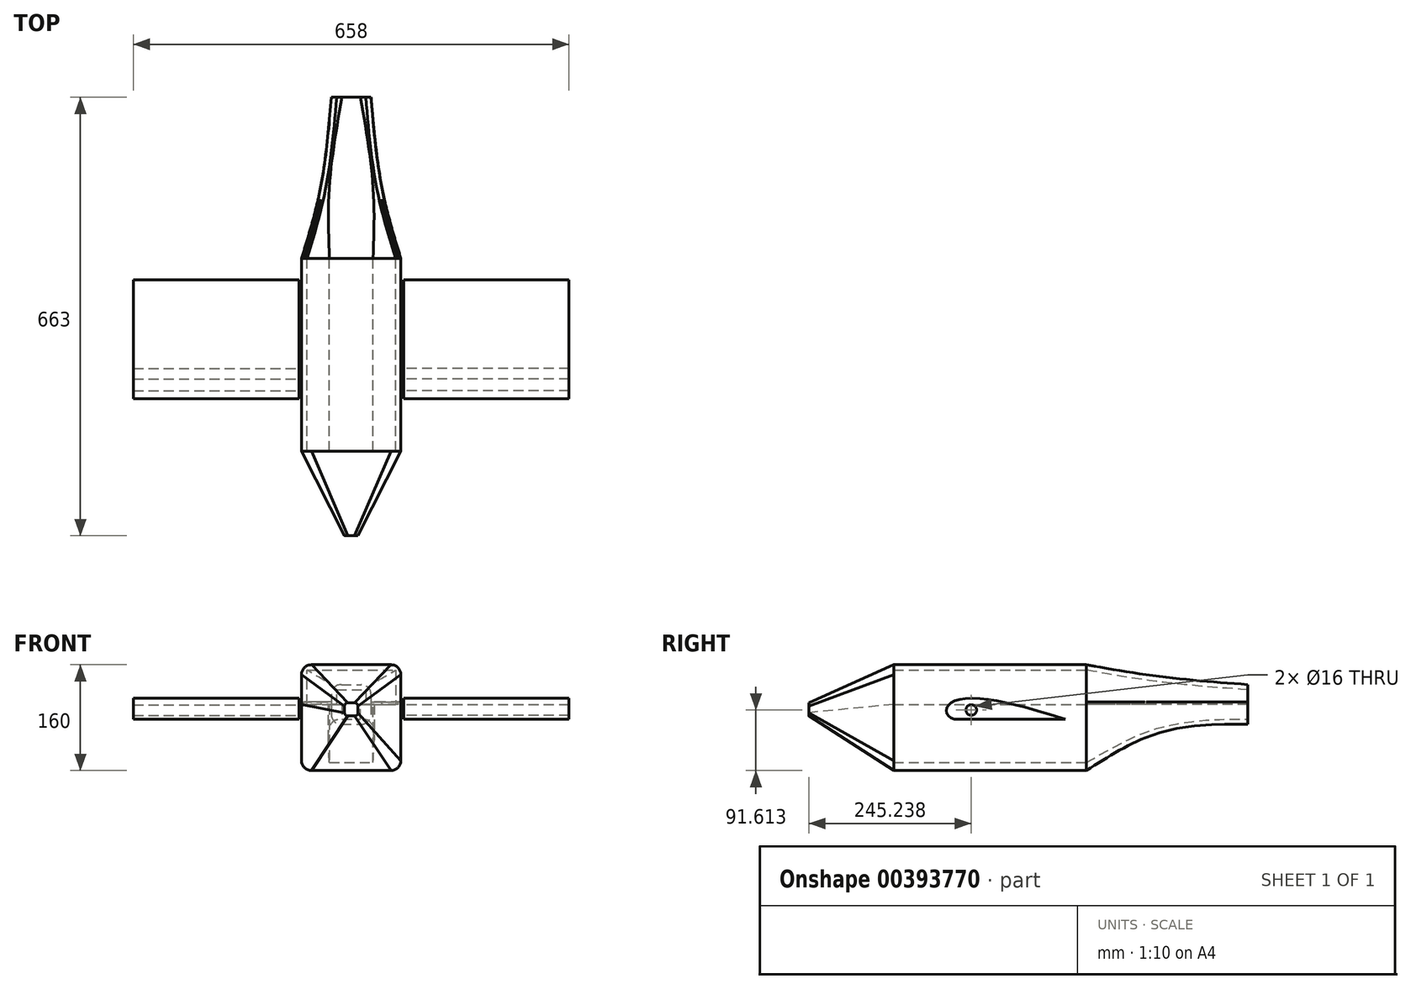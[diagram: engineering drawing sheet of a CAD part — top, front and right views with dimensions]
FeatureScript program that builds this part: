
annotation { "Feature Type Name" : "Feature", "Feature Type Description" : "" }
export const myFeature = defineFeature(function(context is Context, id is Id, definition is map)
    precondition{}
    {
        {
            var Q0;
            Q0=qCreatedBy(makeId("Front.planeOp"),FACE);
            cPlane(context, id + "F0", {"entities" : qUnion([Q0]), "cplaneType" : CPlaneType.OFFSET, "offset" : 154 * mm, "oppositeDirection" : true, "width" : 150 * mm, "height" : 150 * mm});
        }
        {
            var Q0;
            Q0=qCreatedBy(id+"F0.planeOp",FACE);
            var sketch = newSketch(context, id + "F1", { "sketchPlane" : qUnion([Q0])});
            skLineSegment(sketch, "E0.bottom", {"start": v(-15, 37.5) * mm, "end": v(15, 37.5) * mm});
            skLineSegment(sketch, "E0.top", {"start": v(-26, 7.5) * mm, "end": v(-14, 7.5) * mm});
            skLineSegment(sketch, "E0.left", {"start": v(-30, 22.5) * mm, "end": v(-30, 7.5) * mm});
            skLineSegment(sketch, "E0.right", {"start": v(30, 22.5) * mm, "end": v(30, 7.5) * mm});
            skLineSegment(sketch, "E1", {"start": v(0, 97.44) * mm, "end": v(0, -97.44) * mm, "construction": true});
            skLineSegment(sketch, "E2", {"start": v(-121.5, 0) * mm, "end": v(121.5, 0) * mm, "construction": true});
            skPoint(sketch, "E3", {"position": v(0, 0) * mm});
            skPoint(sketch, "E4", {"position": v(0, 37.5) * mm});
            skPoint(sketch, "E5.visualSharp", {"position": v(-30, 37.5) * mm});
            skArc(sketch, "E5.filletArc", {"start": v(-15, 37.5) * mm, "mid": v(-25.6, 33.1) * mm, "end": v(-30, 22.5) * mm});
            skPoint(sketch, "E6.visualSharp", {"position": v(30, 37.5) * mm});
            skArc(sketch, "E6.filletArc", {"start": v(30, 22.5) * mm, "mid": v(25.6, 33.1) * mm, "end": v(15, 37.5) * mm});
            skLineSegment(sketch, "E7", {"start": v(-22, 7.5) * mm, "end": v(-22, 29.5) * mm});
            skLineSegment(sketch, "E8", {"start": v(-22, 29.5) * mm, "end": v(22, 29.5) * mm});
            skLineSegment(sketch, "E9", {"start": v(22, 29.5) * mm, "end": v(22, 7.5) * mm});
            skPoint(sketch, "E10", {"position": v(0, 29.5) * mm});
            skLineSegment(sketch, "E11", {"start": v(-26, 7.5) * mm, "end": v(-26, 11.5) * mm});
            skLineSegment(sketch, "E12", {"start": v(-26, 11.5) * mm, "end": v(-30, 11.5) * mm});
            skLineSegment(sketch, "E13", {"start": v(26, 7.5) * mm, "end": v(26, 11.5) * mm});
            skLineSegment(sketch, "E14", {"start": v(26, 11.5) * mm, "end": v(30, 11.5) * mm});
            skLineSegment(sketch, "E15.top", {"start": v(-15, -22.5) * mm, "end": v(15, -22.5) * mm});
            skLineSegment(sketch, "E15.left", {"start": v(-30, 7.5) * mm, "end": v(-30, -7.5) * mm});
            skLineSegment(sketch, "E15.right", {"start": v(30, 7.5) * mm, "end": v(30, -7.5) * mm});
            skLineSegment(sketch, "E16", {"start": v(-14, 7.5) * mm, "end": v(-14, -14.5) * mm});
            skLineSegment(sketch, "E17", {"start": v(-14, -14.5) * mm, "end": v(14, -14.5) * mm});
            skLineSegment(sketch, "E18", {"start": v(14, -14.5) * mm, "end": v(14, 7.5) * mm});
            skPoint(sketch, "E19", {"position": v(0, -14.5) * mm});
            skPoint(sketch, "E20", {"position": v(0, -22.5) * mm});
            skPoint(sketch, "E21.visualSharp", {"position": v(-30, -22.5) * mm});
            skArc(sketch, "E21.filletArc", {"start": v(-30, -7.5) * mm, "mid": v(-25.6, -18.11) * mm, "end": v(-15, -22.5) * mm});
            skPoint(sketch, "E22.visualSharp", {"position": v(30, -22.5) * mm});
            skArc(sketch, "E22.filletArc", {"start": v(15, -22.5) * mm, "mid": v(25.6, -18.11) * mm, "end": v(30, -7.5) * mm});
            skLineSegment(sketch, "E23.trimOffspring", {"start": v(14, 7.5) * mm, "end": v(26, 7.5) * mm});
            skSolve(sketch);
        }
        {
            var Q0;
            Q0=qCreatedBy(makeId("Front.planeOp"),FACE);
            cPlane(context, id + "F2", {"entities" : qUnion([Q0]), "cplaneType" : CPlaneType.OFFSET, "offset" : 90 * mm, "width" : 150 * mm, "height" : 150 * mm});
        }
        {
            var Q0;
            Q0=qCreatedBy(id+"F2.planeOp",FACE);
            cPlane(context, id + "F3", {"entities" : qUnion([Q0]), "cplaneType" : CPlaneType.OFFSET, "offset" : 111 * mm, "width" : 150 * mm, "height" : 150 * mm});
        }
        {
            var Q0;
            Q0=qCreatedBy(id+"F3.planeOp",FACE);
            cPlane(context, id + "F4", {"entities" : qUnion([Q0]), "cplaneType" : CPlaneType.OFFSET, "offset" : 180 * mm, "width" : 150 * mm, "height" : 150 * mm});
        }
        {
            var Q0;
            Q0=qCreatedBy(makeId("Front.planeOp"),FACE);
            var sketch = newSketch(context, id + "F5", { "sketchPlane" : qUnion([Q0])});
            skLineSegment(sketch, "E24.bottom", {"start": v(-35, 52.5) * mm, "end": v(35, 52.5) * mm});
            skLineSegment(sketch, "E24.top", {"start": v(-46, 7.5) * mm, "end": v(-34, 7.5) * mm});
            skLineSegment(sketch, "E24.left", {"start": v(-50, 37.5) * mm, "end": v(-50, 7.5) * mm});
            skLineSegment(sketch, "E24.right", {"start": v(50, 37.5) * mm, "end": v(50, 7.5) * mm});
            skLineSegment(sketch, "E25", {"start": v(0, 97.44) * mm, "end": v(0, -97.44) * mm, "construction": true});
            skLineSegment(sketch, "E26", {"start": v(-121.5, 0) * mm, "end": v(121.5, 0) * mm, "construction": true});
            skPoint(sketch, "E27", {"position": v(0, 0) * mm});
            skPoint(sketch, "E28", {"position": v(0, 52.5) * mm});
            skPoint(sketch, "E29.visualSharp", {"position": v(-50, 52.5) * mm});
            skArc(sketch, "E29.filletArc", {"start": v(-35, 52.5) * mm, "mid": v(-45.6, 48.1) * mm, "end": v(-50, 37.5) * mm});
            skPoint(sketch, "E30.visualSharp", {"position": v(50, 52.5) * mm});
            skArc(sketch, "E30.filletArc", {"start": v(50, 37.5) * mm, "mid": v(45.6, 48.1) * mm, "end": v(35, 52.5) * mm});
            skLineSegment(sketch, "E31", {"start": v(-42, 7.5) * mm, "end": v(-42, 44.5) * mm});
            skLineSegment(sketch, "E32", {"start": v(-42, 44.5) * mm, "end": v(42, 44.5) * mm});
            skLineSegment(sketch, "E33", {"start": v(42, 44.5) * mm, "end": v(42, 7.5) * mm});
            skPoint(sketch, "E34", {"position": v(0, 44.5) * mm});
            skLineSegment(sketch, "E35", {"start": v(-46, 7.5) * mm, "end": v(-46, 11.5) * mm});
            skLineSegment(sketch, "E36", {"start": v(-46, 11.5) * mm, "end": v(-50, 11.5) * mm});
            skLineSegment(sketch, "E37", {"start": v(46, 7.5) * mm, "end": v(46, 11.5) * mm});
            skLineSegment(sketch, "E38", {"start": v(46, 11.5) * mm, "end": v(50, 11.5) * mm});
            skLineSegment(sketch, "E39.top", {"start": v(-35, -42.5) * mm, "end": v(35, -42.5) * mm});
            skLineSegment(sketch, "E39.left", {"start": v(-50, 7.5) * mm, "end": v(-50, -27.5) * mm});
            skLineSegment(sketch, "E39.right", {"start": v(50, 7.5) * mm, "end": v(50, -27.5) * mm});
            skLineSegment(sketch, "E40", {"start": v(-34, 7.5) * mm, "end": v(-34, -34.5) * mm});
            skLineSegment(sketch, "E41", {"start": v(-34, -34.5) * mm, "end": v(34, -34.5) * mm});
            skLineSegment(sketch, "E42", {"start": v(34, -34.5) * mm, "end": v(34, 7.5) * mm});
            skPoint(sketch, "E43", {"position": v(0, -34.5) * mm});
            skPoint(sketch, "E44", {"position": v(0, -42.5) * mm});
            skPoint(sketch, "E45.visualSharp", {"position": v(-50, -42.5) * mm});
            skArc(sketch, "E45.filletArc", {"start": v(-50, -27.5) * mm, "mid": v(-45.6, -38.11) * mm, "end": v(-35, -42.5) * mm});
            skPoint(sketch, "E46.visualSharp", {"position": v(50, -42.5) * mm});
            skArc(sketch, "E46.filletArc", {"start": v(35, -42.5) * mm, "mid": v(45.6, -38.11) * mm, "end": v(50, -27.5) * mm});
            skLineSegment(sketch, "E47.trimOffspring", {"start": v(34, 7.5) * mm, "end": v(46, 7.5) * mm});
            skSolve(sketch);
        }
        {
            var Q0;
            Q0=qCreatedBy(id+"F2.planeOp",FACE);
            var sketch = newSketch(context, id + "F6", { "sketchPlane" : qUnion([Q0])});
            skLineSegment(sketch, "E48.bottom", {"start": v(-60, 67.5) * mm, "end": v(60, 67.5) * mm});
            skLineSegment(sketch, "E48.top", {"start": v(-71, 7.5) * mm, "end": v(-33, 7.5) * mm});
            skLineSegment(sketch, "E48.left", {"start": v(-75, 52.5) * mm, "end": v(-75, 7.5) * mm});
            skLineSegment(sketch, "E48.right", {"start": v(75, 52.5) * mm, "end": v(75, 7.5) * mm});
            skLineSegment(sketch, "E49", {"start": v(0, 97.44) * mm, "end": v(0, -97.44) * mm, "construction": true});
            skLineSegment(sketch, "E50", {"start": v(-121.5, 0) * mm, "end": v(121.5, 0) * mm, "construction": true});
            skPoint(sketch, "E51", {"position": v(0, 0) * mm});
            skPoint(sketch, "E52", {"position": v(0, 67.5) * mm});
            skPoint(sketch, "E53.visualSharp", {"position": v(-75, 67.5) * mm});
            skArc(sketch, "E53.filletArc", {"start": v(-60, 67.5) * mm, "mid": v(-70.6, 63.1) * mm, "end": v(-75, 52.5) * mm});
            skPoint(sketch, "E54.visualSharp", {"position": v(75, 67.5) * mm});
            skArc(sketch, "E54.filletArc", {"start": v(75, 52.5) * mm, "mid": v(70.6, 63.1) * mm, "end": v(60, 67.5) * mm});
            skLineSegment(sketch, "E55", {"start": v(-67, 7.5) * mm, "end": v(-67, 59.5) * mm});
            skLineSegment(sketch, "E56", {"start": v(-67, 59.5) * mm, "end": v(67, 59.5) * mm});
            skLineSegment(sketch, "E57", {"start": v(67, 59.5) * mm, "end": v(67, 7.5) * mm});
            skPoint(sketch, "E58", {"position": v(0, 59.5) * mm});
            skLineSegment(sketch, "E59", {"start": v(-71, 7.5) * mm, "end": v(-71, 11.5) * mm});
            skLineSegment(sketch, "E60", {"start": v(-71, 11.5) * mm, "end": v(-75, 11.5) * mm});
            skLineSegment(sketch, "E61", {"start": v(71, 7.5) * mm, "end": v(71, 11.5) * mm});
            skLineSegment(sketch, "E62", {"start": v(71, 11.5) * mm, "end": v(75, 11.5) * mm});
            skLineSegment(sketch, "E63.top", {"start": v(-60, -92.5) * mm, "end": v(60, -92.5) * mm});
            skLineSegment(sketch, "E63.left", {"start": v(-75, 7.5) * mm, "end": v(-75, -77.5) * mm});
            skLineSegment(sketch, "E63.right", {"start": v(75, 7.5) * mm, "end": v(75, -77.5) * mm});
            skLineSegment(sketch, "E64", {"start": v(-33, 7.5) * mm, "end": v(-33, -80.5) * mm});
            skLineSegment(sketch, "E65", {"start": v(-33, -80.5) * mm, "end": v(33, -80.5) * mm});
            skLineSegment(sketch, "E66", {"start": v(33, -80.5) * mm, "end": v(33, 7.5) * mm});
            skPoint(sketch, "E67", {"position": v(0, -80.5) * mm});
            skPoint(sketch, "E68", {"position": v(0, -92.5) * mm});
            skPoint(sketch, "E69.visualSharp", {"position": v(-75, -92.5) * mm});
            skArc(sketch, "E69.filletArc", {"start": v(-75, -77.5) * mm, "mid": v(-70.6, -88.11) * mm, "end": v(-60, -92.5) * mm});
            skPoint(sketch, "E70.visualSharp", {"position": v(75, -92.5) * mm});
            skArc(sketch, "E70.filletArc", {"start": v(60, -92.5) * mm, "mid": v(70.6, -88.11) * mm, "end": v(75, -77.5) * mm});
            skLineSegment(sketch, "E71.trimOffspring", {"start": v(33, 7.5) * mm, "end": v(71, 7.5) * mm});
            skSolve(sketch);
        }
        {
            var Q0;
            Q0=qCreatedBy(id+"F3.planeOp",FACE);
            var sketch = newSketch(context, id + "F7", { "sketchPlane" : qUnion([Q0])});
            skLineSegment(sketch, "E72.bottom", {"start": v(-60, 67.5) * mm, "end": v(60, 67.5) * mm});
            skLineSegment(sketch, "E72.top", {"start": v(-71, 7.5) * mm, "end": v(-33, 7.5) * mm});
            skLineSegment(sketch, "E72.left", {"start": v(-75, 52.5) * mm, "end": v(-75, 7.5) * mm});
            skLineSegment(sketch, "E72.right", {"start": v(75, 52.5) * mm, "end": v(75, 7.5) * mm});
            skLineSegment(sketch, "E73", {"start": v(0, 97.44) * mm, "end": v(0, -97.44) * mm, "construction": true});
            skLineSegment(sketch, "E74", {"start": v(-121.5, 0) * mm, "end": v(121.5, 0) * mm, "construction": true});
            skPoint(sketch, "E75", {"position": v(0, 0) * mm});
            skPoint(sketch, "E76", {"position": v(0, 67.5) * mm});
            skPoint(sketch, "E77.visualSharp", {"position": v(-75, 67.5) * mm});
            skArc(sketch, "E77.filletArc", {"start": v(-60, 67.5) * mm, "mid": v(-70.6, 63.1) * mm, "end": v(-75, 52.5) * mm});
            skPoint(sketch, "E78.visualSharp", {"position": v(75, 67.5) * mm});
            skArc(sketch, "E78.filletArc", {"start": v(75, 52.5) * mm, "mid": v(70.6, 63.1) * mm, "end": v(60, 67.5) * mm});
            skLineSegment(sketch, "E79", {"start": v(-67, 7.5) * mm, "end": v(-67, 59.5) * mm});
            skLineSegment(sketch, "E80", {"start": v(-67, 59.5) * mm, "end": v(67, 59.5) * mm});
            skLineSegment(sketch, "E81", {"start": v(67, 59.5) * mm, "end": v(67, 7.5) * mm});
            skPoint(sketch, "E82", {"position": v(0, 59.5) * mm});
            skLineSegment(sketch, "E83", {"start": v(-71, 7.5) * mm, "end": v(-71, 11.5) * mm});
            skLineSegment(sketch, "E84", {"start": v(-71, 11.5) * mm, "end": v(-75, 11.5) * mm});
            skLineSegment(sketch, "E85", {"start": v(71, 7.5) * mm, "end": v(71, 11.5) * mm});
            skLineSegment(sketch, "E86", {"start": v(71, 11.5) * mm, "end": v(75, 11.5) * mm});
            skLineSegment(sketch, "E87.top", {"start": v(-60, -92.5) * mm, "end": v(60, -92.5) * mm});
            skLineSegment(sketch, "E87.left", {"start": v(-75, 7.5) * mm, "end": v(-75, -77.5) * mm});
            skLineSegment(sketch, "E87.right", {"start": v(75, 7.5) * mm, "end": v(75, -77.5) * mm});
            skLineSegment(sketch, "E88", {"start": v(-33, 7.5) * mm, "end": v(-33, -80.5) * mm});
            skLineSegment(sketch, "E89", {"start": v(-33, -80.5) * mm, "end": v(33, -80.5) * mm});
            skLineSegment(sketch, "E90", {"start": v(33, -80.5) * mm, "end": v(33, 7.5) * mm});
            skPoint(sketch, "E91", {"position": v(0, -80.5) * mm});
            skPoint(sketch, "E92", {"position": v(0, -92.5) * mm});
            skPoint(sketch, "E93.visualSharp", {"position": v(-75, -92.5) * mm});
            skArc(sketch, "E93.filletArc", {"start": v(-75, -77.5) * mm, "mid": v(-70.6, -88.11) * mm, "end": v(-60, -92.5) * mm});
            skPoint(sketch, "E94.visualSharp", {"position": v(75, -92.5) * mm});
            skArc(sketch, "E94.filletArc", {"start": v(60, -92.5) * mm, "mid": v(70.6, -88.11) * mm, "end": v(75, -77.5) * mm});
            skLineSegment(sketch, "E95.trimOffspring", {"start": v(33, 7.5) * mm, "end": v(71, 7.5) * mm});
            skSolve(sketch);
        }
        {
            var Q0;
            Q0=qCreatedBy(id+"F4.planeOp",FACE);
            var sketch = newSketch(context, id + "F8", { "sketchPlane" : qUnion([Q0])});
            skLineSegment(sketch, "E96.bottom", {"start": v(-60, 67.5) * mm, "end": v(60, 67.5) * mm});
            skLineSegment(sketch, "E96.top", {"start": v(-71, 7.5) * mm, "end": v(-33, 7.5) * mm});
            skLineSegment(sketch, "E96.left", {"start": v(-75, 52.5) * mm, "end": v(-75, 7.5) * mm});
            skLineSegment(sketch, "E96.right", {"start": v(75, 52.5) * mm, "end": v(75, 7.5) * mm});
            skLineSegment(sketch, "E97", {"start": v(0, 97.44) * mm, "end": v(0, -97.44) * mm, "construction": true});
            skLineSegment(sketch, "E98", {"start": v(-121.5, 0) * mm, "end": v(121.5, 0) * mm, "construction": true});
            skPoint(sketch, "E99", {"position": v(0, 0) * mm});
            skPoint(sketch, "E100", {"position": v(0, 67.5) * mm});
            skPoint(sketch, "E101.visualSharp", {"position": v(-75, 67.5) * mm});
            skArc(sketch, "E101.filletArc", {"start": v(-60, 67.5) * mm, "mid": v(-70.6, 63.1) * mm, "end": v(-75, 52.5) * mm});
            skPoint(sketch, "E102.visualSharp", {"position": v(75, 67.5) * mm});
            skArc(sketch, "E102.filletArc", {"start": v(75, 52.5) * mm, "mid": v(70.6, 63.1) * mm, "end": v(60, 67.5) * mm});
            skLineSegment(sketch, "E103", {"start": v(-67, 7.5) * mm, "end": v(-67, 59.5) * mm});
            skLineSegment(sketch, "E104", {"start": v(-67, 59.5) * mm, "end": v(67, 59.5) * mm});
            skLineSegment(sketch, "E105", {"start": v(67, 59.5) * mm, "end": v(67, 7.5) * mm});
            skPoint(sketch, "E106", {"position": v(0, 59.5) * mm});
            skLineSegment(sketch, "E107", {"start": v(-71, 7.5) * mm, "end": v(-71, 11.5) * mm});
            skLineSegment(sketch, "E108", {"start": v(-71, 11.5) * mm, "end": v(-75, 11.5) * mm});
            skLineSegment(sketch, "E109", {"start": v(71, 7.5) * mm, "end": v(71, 11.5) * mm});
            skLineSegment(sketch, "E110", {"start": v(71, 11.5) * mm, "end": v(75, 11.5) * mm});
            skLineSegment(sketch, "E111.top", {"start": v(-60, -92.5) * mm, "end": v(60, -92.5) * mm});
            skLineSegment(sketch, "E111.left", {"start": v(-75, 7.5) * mm, "end": v(-75, -77.5) * mm});
            skLineSegment(sketch, "E111.right", {"start": v(75, 7.5) * mm, "end": v(75, -77.5) * mm});
            skLineSegment(sketch, "E112", {"start": v(-33, 7.5) * mm, "end": v(-33, -80.5) * mm});
            skLineSegment(sketch, "E113", {"start": v(-33, -80.5) * mm, "end": v(33, -80.5) * mm});
            skLineSegment(sketch, "E114", {"start": v(33, -80.5) * mm, "end": v(33, 7.5) * mm});
            skPoint(sketch, "E115", {"position": v(0, -80.5) * mm});
            skPoint(sketch, "E116", {"position": v(0, -92.5) * mm});
            skPoint(sketch, "E117.visualSharp", {"position": v(-75, -92.5) * mm});
            skArc(sketch, "E117.filletArc", {"start": v(-75, -77.5) * mm, "mid": v(-70.6, -88.11) * mm, "end": v(-60, -92.5) * mm});
            skPoint(sketch, "E118.visualSharp", {"position": v(75, -92.5) * mm});
            skArc(sketch, "E118.filletArc", {"start": v(60, -92.5) * mm, "mid": v(70.6, -88.11) * mm, "end": v(75, -77.5) * mm});
            skLineSegment(sketch, "E119.trimOffspring", {"start": v(33, 7.5) * mm, "end": v(71, 7.5) * mm});
            skSolve(sketch);
        }
        {
            var Q0;
            Q0=makeQuery(id+"F1.imprint","IMPRINT",FACE,{"disambiguationData":[TD([[makeQuery(id+"F1.imprint","IMPRINT",EDGE,{"derivedFrom":sQuery(id+"F1.wireOp",EDGE,"E0.bottom")}),-1.0]])]});
            var Q1;
            Q1=makeQuery(id+"F5.imprint","IMPRINT",FACE,{"disambiguationData":[TD([[makeQuery(id+"F5.imprint","IMPRINT",EDGE,{"derivedFrom":sQuery(id+"F5.wireOp",EDGE,"E24.bottom")}),-1.0]])]});
            var Q2;
            Q2=makeQuery(id+"F6.imprint","IMPRINT",FACE,{"disambiguationData":[TD([[makeQuery(id+"F6.imprint","IMPRINT",EDGE,{"derivedFrom":sQuery(id+"F6.wireOp",EDGE,"E48.bottom")}),-1.0]])]});
            loft(context, id + "F9", {"sheetProfilesArray" : [{ "sheetProfileEntities" : qUnion([Q0]) }, { "sheetProfileEntities" : qUnion([Q1]) }, { "sheetProfileEntities" : qUnion([Q2]) }]});
        }
        {
            var Q0;
            Q0=makeQuery(id+"F8.imprint","IMPRINT",FACE,{"disambiguationData":[TD([[makeQuery(id+"F8.imprint","IMPRINT",EDGE,{"derivedFrom":sQuery(id+"F8.wireOp",EDGE,"E96.bottom")}),-1.0]])]});
            var Q1;
            Q1=makeQuery(id+"F7.imprint","IMPRINT",FACE,{"disambiguationData":[TD([[makeQuery(id+"F7.imprint","IMPRINT",EDGE,{"derivedFrom":sQuery(id+"F7.wireOp",EDGE,"E72.bottom")}),-1.0]])]});
            var Q2;
            Q2=makeQuery(id+"F6.imprint","IMPRINT",FACE,{"disambiguationData":[TD([[makeQuery(id+"F6.imprint","IMPRINT",EDGE,{"derivedFrom":sQuery(id+"F6.wireOp",EDGE,"E48.bottom")}),-1.0]])]});
            loft(context, id + "F10", {"sheetProfilesArray" : [{ "sheetProfileEntities" : qUnion([Q0]) }, { "sheetProfileEntities" : qUnion([Q1]) }, { "sheetProfileEntities" : qUnion([Q2]) }]});
        }
        {
            var Q1;
            {var subQ3=sQuery(id+"F8.wireOp",EDGE,"E107");Q1=makeQuery(id+"F8.imprint","IMPRINT",FACE,{"disambiguationData":[TD([[makeQuery(id+"F8.imprint","IMPRINT",EDGE,{"derivedFrom":subQ3}),1.0]])]});}
            var Q2;
            {var subQ3=sQuery(id+"F7.wireOp",EDGE,"E83");Q2=makeQuery(id+"F7.imprint","IMPRINT",FACE,{"disambiguationData":[TD([[makeQuery(id+"F7.imprint","IMPRINT",EDGE,{"derivedFrom":subQ3}),1.0]])]});}
            var Q3;
            {var subQ3=sQuery(id+"F6.wireOp",EDGE,"E59");Q3=makeQuery(id+"F6.imprint","IMPRINT",FACE,{"disambiguationData":[TD([[makeQuery(id+"F6.imprint","IMPRINT",EDGE,{"derivedFrom":subQ3}),1.0]])]});}
            loft(context, id + "F11", {"sheetProfilesArray" : [{ "sheetProfileEntities" : qUnion([Q1]) }, { "sheetProfileEntities" : qUnion([Q2]) }, { "sheetProfileEntities" : qUnion([Q3]) }]});
        }
        {
            var Q1;
            {var subQ3=sQuery(id+"F6.wireOp",EDGE,"E59");Q1=makeQuery(id+"F6.imprint","IMPRINT",FACE,{"disambiguationData":[TD([[makeQuery(id+"F6.imprint","IMPRINT",EDGE,{"derivedFrom":subQ3}),1.0]])]});}
            var Q2;
            {var subQ3=sQuery(id+"F5.wireOp",EDGE,"E35");Q2=makeQuery(id+"F5.imprint","IMPRINT",FACE,{"disambiguationData":[TD([[makeQuery(id+"F5.imprint","IMPRINT",EDGE,{"derivedFrom":subQ3}),1.0]])]});}
            var Q3;
            {var subQ3=sQuery(id+"F1.wireOp",EDGE,"E11");Q3=makeQuery(id+"F1.imprint","IMPRINT",FACE,{"disambiguationData":[TD([[makeQuery(id+"F1.imprint","IMPRINT",EDGE,{"derivedFrom":subQ3}),1.0]])]});}
            loft(context, id + "F12", {"operationType" : NewBodyOperationType.ADD, "sheetProfilesArray" : [{ "sheetProfileEntities" : qUnion([Q1]) }, { "sheetProfileEntities" : qUnion([Q2]) }, { "sheetProfileEntities" : qUnion([Q3]) }]});
        }
        {
            var Q0;
            Q0=qCreatedBy(id+"F4.planeOp",FACE);
            cPlane(context, id + "F13", {"entities" : qUnion([Q0]), "cplaneType" : CPlaneType.OFFSET, "offset" : 0 * mm, "width" : 150 * mm, "height" : 150 * mm});
        }
        {
            var Q0;
            Q0=qCreatedBy(id+"F13.planeOp",FACE);
            cPlane(context, id + "F14", {"entities" : qUnion([Q0]), "cplaneType" : CPlaneType.OFFSET, "offset" : 128 * mm, "width" : 150 * mm, "height" : 150 * mm});
        }
        {
            var Q0;
            Q0=qCreatedBy(id+"F14.planeOp",FACE);
            var sketch = newSketch(context, id + "F15", { "sketchPlane" : qUnion([Q0])});
            skLineSegment(sketch, "E120.bottom", {"start": v(-5, 10) * mm, "end": v(5, 10) * mm});
            skLineSegment(sketch, "E120.top", {"start": v(-5, -10) * mm, "end": v(5, -10) * mm});
            skLineSegment(sketch, "E120.left", {"start": v(-10, 5) * mm, "end": v(-10, -5) * mm});
            skLineSegment(sketch, "E120.right", {"start": v(10, 5) * mm, "end": v(10, -5) * mm});
            skPoint(sketch, "E121", {"position": v(10, 0) * mm});
            skPoint(sketch, "E122", {"position": v(0, 10) * mm});
            skLineSegment(sketch, "E123", {"start": v(0, 98.17) * mm, "end": v(0, -98.06) * mm, "construction": true});
            skLineSegment(sketch, "E124", {"start": v(-119.52, 0) * mm, "end": v(125.33, 0) * mm, "construction": true});
            skPoint(sketch, "E125.visualSharp", {"position": v(-10, 10) * mm});
            skArc(sketch, "E125.filletArc", {"start": v(-5, 10) * mm, "mid": v(-8.54, 8.54) * mm, "end": v(-10, 5) * mm});
            skPoint(sketch, "E126.visualSharp", {"position": v(10, 10) * mm});
            skArc(sketch, "E126.filletArc", {"start": v(10, 5) * mm, "mid": v(8.54, 8.54) * mm, "end": v(5, 10) * mm});
            skPoint(sketch, "E127.visualSharp", {"position": v(-10, -10) * mm});
            skArc(sketch, "E127.filletArc", {"start": v(-10, -5) * mm, "mid": v(-8.54, -8.54) * mm, "end": v(-5, -10) * mm});
            skPoint(sketch, "E128.visualSharp", {"position": v(10, -10) * mm});
            skArc(sketch, "E128.filletArc", {"start": v(5, -10) * mm, "mid": v(8.54, -8.54) * mm, "end": v(10, -5) * mm});
            skSolve(sketch);
        }
        {
            var Q0;
            Q0=qCreatedBy(id+"F13.planeOp",FACE);
            var sketch = newSketch(context, id + "F16", { "sketchPlane" : qUnion([Q0])});
            skLineSegment(sketch, "E129.bottom", {"start": v(-60, 67.5) * mm, "end": v(60, 67.5) * mm});
            skLineSegment(sketch, "E129.left", {"start": v(-75, 52.5) * mm, "end": v(-75, 7.5) * mm});
            skLineSegment(sketch, "E129.right", {"start": v(75, 52.5) * mm, "end": v(75, 7.5) * mm});
            skLineSegment(sketch, "E130", {"start": v(0, 97.44) * mm, "end": v(0, -97.44) * mm, "construction": true});
            skLineSegment(sketch, "E131", {"start": v(-121.5, 0) * mm, "end": v(121.5, 0) * mm, "construction": true});
            skPoint(sketch, "E132", {"position": v(0, 0) * mm});
            skPoint(sketch, "E133", {"position": v(0, 67.5) * mm});
            skPoint(sketch, "E134.visualSharp", {"position": v(-75, 67.5) * mm});
            skArc(sketch, "E134.filletArc", {"start": v(-60, 67.5) * mm, "mid": v(-70.6, 63.1) * mm, "end": v(-75, 52.5) * mm});
            skPoint(sketch, "E135.visualSharp", {"position": v(75, 67.5) * mm});
            skArc(sketch, "E135.filletArc", {"start": v(75, 52.5) * mm, "mid": v(70.6, 63.1) * mm, "end": v(60, 67.5) * mm});
            skPoint(sketch, "E136", {"position": v(0, 59.5) * mm});
            skLineSegment(sketch, "E137.top", {"start": v(-60, -92.5) * mm, "end": v(60, -92.5) * mm});
            skLineSegment(sketch, "E137.left", {"start": v(-75, 7.5) * mm, "end": v(-75, -77.5) * mm});
            skLineSegment(sketch, "E137.right", {"start": v(75, 7.5) * mm, "end": v(75, -77.5) * mm});
            skPoint(sketch, "E138", {"position": v(0, -84.5) * mm});
            skPoint(sketch, "E139", {"position": v(0, -92.5) * mm});
            skPoint(sketch, "E140.visualSharp", {"position": v(-75, -92.5) * mm});
            skArc(sketch, "E140.filletArc", {"start": v(-75, -77.5) * mm, "mid": v(-70.6, -88.11) * mm, "end": v(-60, -92.5) * mm});
            skPoint(sketch, "E141.visualSharp", {"position": v(75, -92.5) * mm});
            skArc(sketch, "E141.filletArc", {"start": v(60, -92.5) * mm, "mid": v(70.6, -88.11) * mm, "end": v(75, -77.5) * mm});
            skSolve(sketch);
        }
        {
            var Q0;
            Q0 = qSketchRegion(id + "F16", true);
            var Q1;
            Q1 = qSketchRegion(id + "F15", true);
            loft(context, id + "F17", {"sheetProfilesArray" : [{ "sheetProfileEntities" : qUnion([Q0]) }, { "sheetProfileEntities" : qUnion([Q1]) }]});
        }
        {
            var Q0;
            Q0=qCreatedBy(makeId("Top.planeOp"),FACE);
            cPlane(context, id + "F18", {"entities" : qUnion([Q0]), "cplaneType" : CPlaneType.OFFSET, "offset" : 25 * mm, "width" : 150 * mm, "height" : 150 * mm});
        }
        {
            var Q0;
            Q0=qCreatedBy(makeId("Right.planeOp"),FACE);
            cPlane(context, id + "F19", {"entities" : qUnion([Q0]), "cplaneType" : CPlaneType.OFFSET, "offset" : 79 * mm, "width" : 150 * mm, "height" : 150 * mm});
        }
        {
            var Q0;
            Q0=qCreatedBy(id+"F19.planeOp",FACE);
            var sketch = newSketch(context, id + "F20", { "sketchPlane" : qUnion([Q0])});
            skLineSegment(sketch, "E142", {"start": v(-46.88, -4.2) * mm, "end": v(10.07, -4.2) * mm, "construction": true});
            skLineSegment(sketch, "E143", {"start": v(-148.76, 116.83) * mm, "end": v(-148.76, -113.4) * mm, "construction": true});
            skPoint(sketch, "E144", {"position": v(0, 0) * mm});
            skPoint(sketch, "E145", {"position": v(-148.76, -4.2) * mm});
            skCircle(sketch, "E146", {"center": v(-148.76, 7.3) * mm, "radius": 8 * mm});
            skLineSegment(sketch, "E147", {"start": v(0, 7.3) * mm, "end": v(-336.64, 7.3) * mm, "construction": true});
            skLineSegment(sketch, "E148", {"start": v(-156.76, 50.6) * mm, "end": v(-156.76, -13.87) * mm, "construction": true});
            skLineSegment(sketch, "E149", {"start": v(-186.76, 51.67) * mm, "end": v(-186.76, -16.38) * mm, "construction": true});
            skLineSegment(sketch, "E150", {"start": v(-6.76, 46.5) * mm, "end": v(-6.76, -13.17) * mm, "construction": true});
            skLineSegment(sketch, "E151", {"start": v(-344.89, -6.7) * mm, "end": v(61.32, -6.7) * mm, "construction": true});
            skLineSegment(sketch, "E152", {"start": v(-352.6, 25.3) * mm, "end": v(117.2, 25.3) * mm, "construction": true});
            skFitSpline(sketch, "E153", {"points": [v(-6.76, -6.7) * mm, v(-148.76, 25.3) * mm, v(-186.5, 8.07) * mm, v(-174.44, -6.7) * mm], "startDerivative": vector(-119.4, 35.58) * mm, "endDerivative": vector(131.78, -26.98) * mm});
            skLineSegment(sketch, "E154", {"start": v(-174.44, -6.7) * mm, "end": v(-6.76, -6.7) * mm});
            skSolve(sketch);
        }
        {
            var Q0;
            Q0=makeQuery(id+"F20.imprint","IMPRINT",FACE,{"disambiguationData":[TD([[makeQuery(id+"F20.imprint","IMPRINT",EDGE,{"derivedFrom":sQuery(id+"F20.wireOp",EDGE,"E146")}),-1.0]])]});
            var Q1;
            Q1 = qSketchRegion(id + "F20", true);
            extrude(context, id + "F21", {"entities" : qUnion([Q0, Q1]), "depth" : 250 * mm});
        }
        {
            var Q0;
            Q0=makeQuery(id+"F21.opExtrude","SWEPT_BODY",BODY,{"disambiguationData":[OSD([sQuery(id+"F20.wireOp",EDGE,"E146"),sQuery(id+"F20.wireOp",EDGE,"E153"),sQuery(id+"F20.wireOp",EDGE,"E154")])]});
            var Q1;
            Q1=qCreatedBy(makeId("Right.planeOp"),FACE);
            mirror(context, id + "F22", {"entities" : qUnion([Q0]), "mirrorPlane" : qUnion([Q1])});
        }
        {
            var Q0;
            Q0=qCreatedBy(id+"F18.planeOp",FACE);
            var sketch = newSketch(context, id + "F23", { "sketchPlane" : qUnion([Q0])});
            skLineSegment(sketch, "E155", {"start": v(0.96, 264.9) * mm, "end": v(0.96, -125.89) * mm, "construction": true});
            skLineSegment(sketch, "E156", {"start": v(-346.3, 70.67) * mm, "end": v(357.96, 70.67) * mm, "construction": true});
            skLineSegment(sketch, "E157", {"start": v(-20.53, -129.33) * mm, "end": v(0.96, -129.33) * mm});
            skLineSegment(sketch, "E158.MirrorCS", {"start": v(22.46, -129.33) * mm, "end": v(0.96, -129.33) * mm});
            skLineSegment(sketch, "E159", {"start": v(-64.58, -39.33) * mm, "end": v(68.96, -39.33) * mm, "construction": true});
            skLineSegment(sketch, "E160", {"start": v(0.96, 90.67) * mm, "end": v(-67.04, 90.67) * mm});
            skLineSegment(sketch, "E161", {"start": v(-67.04, 90.67) * mm, "end": v(-67.04, -39.33) * mm});
            skLineSegment(sketch, "E162", {"start": v(-40.54, -129.33) * mm, "end": v(42.47, -129.33) * mm});
            skPoint(sketch, "E163", {"position": v(0.96, -129.33) * mm});
            skArc(sketch, "E164", {"start": v(-40.54, -129.33) * mm, "mid": v(-48.96, -82.91) * mm, "end": v(-67.04, -39.33) * mm});
            skArc(sketch, "E165.MirrorCS", {"start": v(42.47, -129.33) * mm, "mid": v(50.88, -82.91) * mm, "end": v(68.96, -39.33) * mm});
            skPoint(sketch, "E166.start.orphan", {"position": v(74.06, -39.33) * mm});
            skLineSegment(sketch, "E167.MirrorCS", {"start": v(0.96, 90.67) * mm, "end": v(68.96, 90.67) * mm});
            skLineSegment(sketch, "E168.MirrorCS", {"start": v(68.96, 90.67) * mm, "end": v(68.96, -39.33) * mm});
            skSolve(sketch);
        }
        {
            var Q0;
            Q0 = qSketchRegion(id + "F23", true);
            extrude(context, id + "F24", {"entities" : qUnion([Q0]), "depth" : 22 * mm});
        }
        {
            var Q0;
            Q0=makeQuery(id+"F24.opExtrude","SWEPT_BODY",BODY,{"disambiguationData":[OSD([sQuery(id+"F23.wireOp",EDGE,"E160"),sQuery(id+"F23.wireOp",EDGE,"E161"),sQuery(id+"F23.wireOp",EDGE,"E162"),sQuery(id+"F23.wireOp",EDGE,"E164"),sQuery(id+"F23.wireOp",EDGE,"E165.MirrorCS"),sQuery(id+"F23.wireOp",EDGE,"E167.MirrorCS"),sQuery(id+"F23.wireOp",EDGE,"E168.MirrorCS")])]});
            var Q1;
            Q1=sQuery(id+"F1.wireOp",EDGE,"E1");
            transform(context, id + "F25", {"entities" : qUnion([Q0]), "transformType" : TransformType.ROTATION, "transformAxis" : qUnion([Q1]), "angle" : 180 * degree, "makeCopy" : false});
        }
        {
            var Q0;
            Q0=makeQuery(id+"F24.opExtrude","SWEPT_BODY",BODY,{"disambiguationData":[OSD([sQuery(id+"F23.wireOp",EDGE,"E160"),sQuery(id+"F23.wireOp",EDGE,"E161"),sQuery(id+"F23.wireOp",EDGE,"E162"),sQuery(id+"F23.wireOp",EDGE,"E164"),sQuery(id+"F23.wireOp",EDGE,"E165.MirrorCS"),sQuery(id+"F23.wireOp",EDGE,"E167.MirrorCS"),sQuery(id+"F23.wireOp",EDGE,"E168.MirrorCS")])]});
            transform(context, id + "F26", {"entities" : qUnion([Q0]), "transformType" : TransformType.TRANSLATION_3D, "dx" : 1.3 * mm, "dy" : -439 * mm, "dz" : 0 * mm, "makeCopy" : false});
        }
        {
            var Q0;
            Q0=makeQuery(id+"F24.opExtrude","SWEPT_BODY",BODY,{"disambiguationData":[OSD([sQuery(id+"F23.wireOp",EDGE,"E160"),sQuery(id+"F23.wireOp",EDGE,"E161"),sQuery(id+"F23.wireOp",EDGE,"E162"),sQuery(id+"F23.wireOp",EDGE,"E164"),sQuery(id+"F23.wireOp",EDGE,"E165.MirrorCS"),sQuery(id+"F23.wireOp",EDGE,"E167.MirrorCS"),sQuery(id+"F23.wireOp",EDGE,"E168.MirrorCS")])]});
            transform(context, id + "F27", {"entities" : qUnion([Q0]), "transformType" : TransformType.TRANSLATION_3D, "dx" : -0.4 * mm, "dy" : -79 * mm, "dz" : 0 * mm, "makeCopy" : false});
        }
        {
            var Q0;
            Q0=makeQuery(id+"F22.opPattern","COPY",BODY,{"derivedFrom":makeQuery(id+"F21.opExtrude","SWEPT_BODY",BODY,{"disambiguationData":[OSD([sQuery(id+"F20.wireOp",EDGE,"E146"),sQuery(id+"F20.wireOp",EDGE,"E153"),sQuery(id+"F20.wireOp",EDGE,"E154")])]}),"instanceName":"1"});
            var Q1;
            Q1=makeQuery(id+"F21.opExtrude","SWEPT_BODY",BODY,{"disambiguationData":[OSD([sQuery(id+"F20.wireOp",EDGE,"E146"),sQuery(id+"F20.wireOp",EDGE,"E153"),sQuery(id+"F20.wireOp",EDGE,"E154")])]});
            transform(context, id + "F28", {"entities" : qUnion([Q0, Q1]), "transformType" : TransformType.TRANSLATION_3D, "dx" : 0 * mm, "dy" : -115 * mm, "dz" : 0 * mm, "makeCopy" : false});
        }
        {
            var Q0;
            Q0=makeQuery(id+"F24.opExtrude","SWEPT_BODY",BODY,{"disambiguationData":[OSD([sQuery(id+"F23.wireOp",EDGE,"E160"),sQuery(id+"F23.wireOp",EDGE,"E161"),sQuery(id+"F23.wireOp",EDGE,"E162"),sQuery(id+"F23.wireOp",EDGE,"E164"),sQuery(id+"F23.wireOp",EDGE,"E165.MirrorCS"),sQuery(id+"F23.wireOp",EDGE,"E167.MirrorCS"),sQuery(id+"F23.wireOp",EDGE,"E168.MirrorCS")])]});
            transform(context, id + "F29", {"entities" : qUnion([Q0]), "transformType" : TransformType.TRANSLATION_3D, "dx" : 0 * mm, "dy" : 0 * mm, "dz" : -48 * mm, "makeCopy" : false});
        }
        {
            var Q0;
            Q0=makeQuery(id+"F24.opExtrude","SWEPT_BODY",BODY,{"disambiguationData":[OSD([sQuery(id+"F23.wireOp",EDGE,"E160"),sQuery(id+"F23.wireOp",EDGE,"E161"),sQuery(id+"F23.wireOp",EDGE,"E162"),sQuery(id+"F23.wireOp",EDGE,"E164"),sQuery(id+"F23.wireOp",EDGE,"E165.MirrorCS"),sQuery(id+"F23.wireOp",EDGE,"E167.MirrorCS"),sQuery(id+"F23.wireOp",EDGE,"E168.MirrorCS")])]});
            transform(context, id + "F30", {"entities" : qUnion([Q0]), "transformType" : TransformType.TRANSLATION_3D, "dx" : 0 * mm, "dy" : 0 * mm, "dz" : 19 * mm, "makeCopy" : false});
        }
        {
            var Q0;
            Q0=makeQuery(id+"F24.opExtrude","SWEPT_BODY",BODY,{"disambiguationData":[OSD([sQuery(id+"F23.wireOp",EDGE,"E160"),sQuery(id+"F23.wireOp",EDGE,"E161"),sQuery(id+"F23.wireOp",EDGE,"E162"),sQuery(id+"F23.wireOp",EDGE,"E164"),sQuery(id+"F23.wireOp",EDGE,"E165.MirrorCS"),sQuery(id+"F23.wireOp",EDGE,"E167.MirrorCS"),sQuery(id+"F23.wireOp",EDGE,"E168.MirrorCS")])]});
            var Q1;
            Q1=makeQuery(id+"F21.opExtrude","SWEPT_BODY",BODY,{"disambiguationData":[OSD([sQuery(id+"F20.wireOp",EDGE,"E146"),sQuery(id+"F20.wireOp",EDGE,"E153"),sQuery(id+"F20.wireOp",EDGE,"E154")])]});
            var Q2;
            Q2=makeQuery(id+"F22.opPattern","COPY",BODY,{"derivedFrom":makeQuery(id+"F21.opExtrude","SWEPT_BODY",BODY,{"disambiguationData":[OSD([sQuery(id+"F20.wireOp",EDGE,"E146"),sQuery(id+"F20.wireOp",EDGE,"E153"),sQuery(id+"F20.wireOp",EDGE,"E154")])]}),"instanceName":"1"});
            transform(context, id + "F31", {"entities" : qUnion([Q0, Q1, Q2]), "transformType" : TransformType.TRANSLATION_3D, "dx" : 0 * mm, "dy" : 0 * mm, "dz" : -8.2 * mm, "makeCopy" : false});
        }
        {
            var Q0;
            Q0=makeQuery(id+"F24.opExtrude","SWEPT_BODY",BODY,{"disambiguationData":[OSD([sQuery(id+"F23.wireOp",EDGE,"E160"),sQuery(id+"F23.wireOp",EDGE,"E161"),sQuery(id+"F23.wireOp",EDGE,"E162"),sQuery(id+"F23.wireOp",EDGE,"E164"),sQuery(id+"F23.wireOp",EDGE,"E165.MirrorCS"),sQuery(id+"F23.wireOp",EDGE,"E167.MirrorCS"),sQuery(id+"F23.wireOp",EDGE,"E168.MirrorCS")])]});
            var Q1;
            Q1=makeQuery(id+"F17.opLoft","SWEPT_BODY",BODY,{"disambiguationData":[OSD([makeQuery(id+"F15.imprint","IMPRINT",FACE,{"disambiguationData":[TD([[makeQuery(id+"F15.imprint","IMPRINT",EDGE,{"derivedFrom":sQuery(id+"F15.wireOp",EDGE,"E120.bottom")}),-1.0]])]}),makeQuery(id+"F16.imprint","IMPRINT",FACE,{"disambiguationData":[TD([[makeQuery(id+"F16.imprint","IMPRINT",EDGE,{"derivedFrom":sQuery(id+"F16.wireOp",EDGE,"E129.bottom")}),-1.0]])]})])]});
            booleanBodies(context, id + "F32", {"operationType" : BooleanOperationType.SUBTRACTION, "tools" : qUnion([Q0]), "targets" : qUnion([Q1])});
        }
    });
